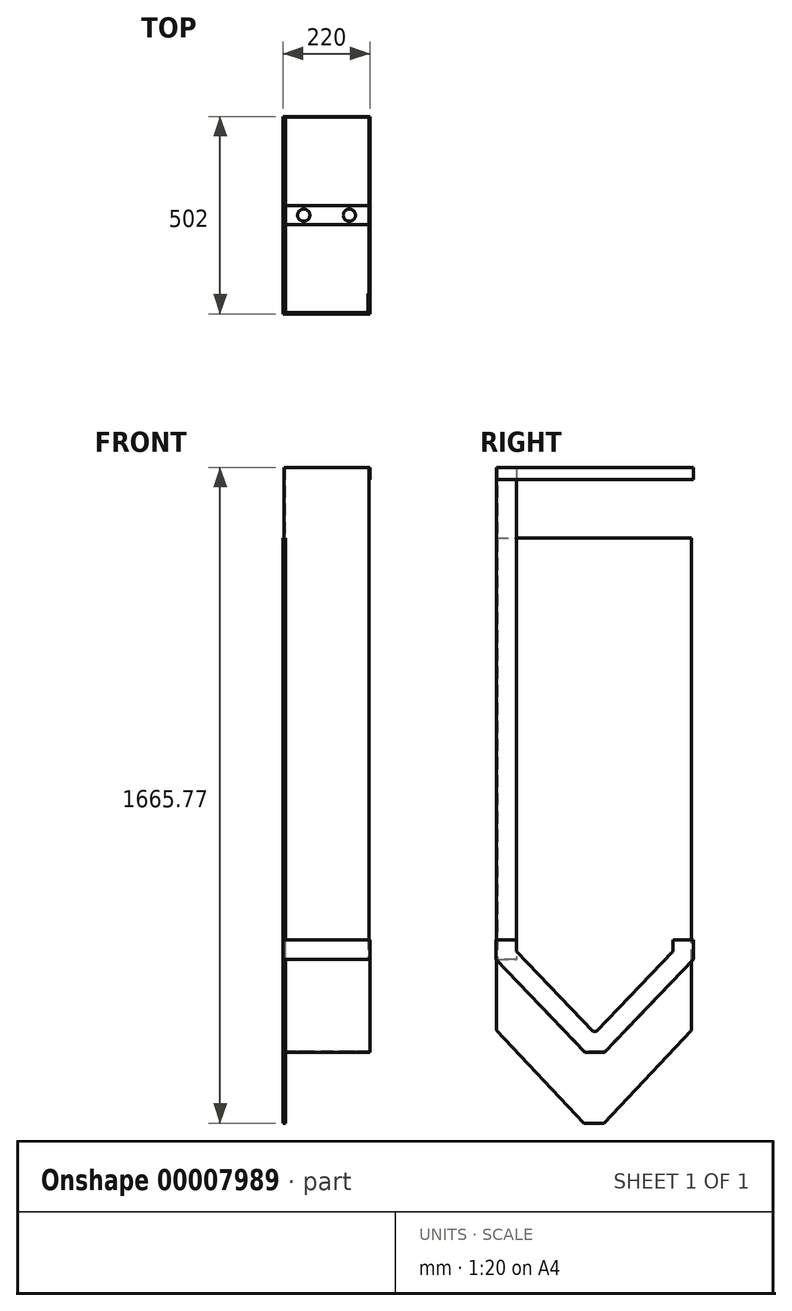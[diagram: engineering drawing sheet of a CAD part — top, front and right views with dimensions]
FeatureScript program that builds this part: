
annotation { "Feature Type Name" : "Feature", "Feature Type Description" : "" }
export const myFeature = defineFeature(function(context is Context, id is Id, definition is map)
    precondition{}
    {
        {
            var Q0;
            Q0=qCreatedBy(makeId("Right.planeOp"),FACE);
            var sketch = newSketch(context, id + "F0", { "sketchPlane" : qUnion([Q0])});
            skLineSegment(sketch, "E0", {"start": v(949.6, -192.94) * mm, "end": v(949.6, -142.94) * mm});
            skLineSegment(sketch, "E1", {"start": v(949.6, -192.94) * mm, "end": v(723.6, -428.58) * mm});
            skLineSegment(sketch, "E2", {"start": v(723.6, -428.58) * mm, "end": v(698.6, -428.58) * mm});
            skLineSegment(sketch, "E3", {"start": v(949.6, -142.94) * mm, "end": v(947.6, -142.94) * mm});
            skLineSegment(sketch, "E4", {"start": v(947.6, -142.94) * mm, "end": v(947.6, -192.13) * mm});
            skLineSegment(sketch, "E5", {"start": v(947.6, -192.13) * mm, "end": v(722.74, -426.58) * mm});
            skLineSegment(sketch, "E6", {"start": v(722.74, -426.58) * mm, "end": v(698.6, -426.58) * mm});
            skLineSegment(sketch, "E7", {"start": v(698.6, -426.58) * mm, "end": v(698.6, -390.33) * mm, "construction": true});
            skLineSegment(sketch, "E8", {"start": v(698.6, -426.58) * mm, "end": v(698.6, -449.98) * mm});
            skLineSegment(sketch, "E9.MirrorCS", {"start": v(673.6, -428.58) * mm, "end": v(698.6, -428.58) * mm});
            skLineSegment(sketch, "E10.MirrorCS", {"start": v(674.45, -426.58) * mm, "end": v(698.6, -426.58) * mm});
            skLineSegment(sketch, "E11.MirrorCS", {"start": v(449.6, -192.13) * mm, "end": v(674.45, -426.58) * mm});
            skLineSegment(sketch, "E12.MirrorCS", {"start": v(447.6, -192.94) * mm, "end": v(673.6, -428.58) * mm});
            skLineSegment(sketch, "E13.MirrorCS", {"start": v(449.6, -142.94) * mm, "end": v(449.6, -192.13) * mm});
            skLineSegment(sketch, "E14.MirrorCS", {"start": v(447.6, -192.94) * mm, "end": v(447.6, -142.94) * mm});
            skLineSegment(sketch, "E15.MirrorCS", {"start": v(447.6, -142.94) * mm, "end": v(449.6, -142.94) * mm});
            skSolve(sketch);
        }
        {
            var Q0;
            Q0=makeQuery(id+"F0.imprint","IMPRINT",FACE,{"disambiguationData":[TD([[makeQuery(id+"F0.imprint","IMPRINT",EDGE,{"derivedFrom":sQuery(id+"F0.wireOp",EDGE,"E0")}),1.0]])]});
            var Q1;
            {var subQ1=sQuery(id+"F0.wireOp",EDGE,"E9.MirrorCS");Q1=makeQuery(id+"F0.imprint","IMPRINT",FACE,{"disambiguationData":[TD([[makeQuery(id+"F0.imprint","IMPRINT",EDGE,{"derivedFrom":subQ1}),1.0]])]});}
            extrude(context, id + "F1", {"entities" : qUnion([Q0, Q1]), "depth" : 220 * mm});
        }
        {
            var Q0;
            Q0=qCreatedBy(makeId("Right.planeOp"),FACE);
            var sketch = newSketch(context, id + "F2", { "sketchPlane" : qUnion([Q0])});
            skLineSegment(sketch, "E16", {"start": v(947.6, -142.94) * mm, "end": v(897.6, -142.94) * mm});
            skLineSegment(sketch, "E17", {"start": v(898.91, -170.66) * mm, "end": v(702.8, -375.14) * mm});
            skLineSegment(sketch, "E18", {"start": v(698.6, -348.8) * mm, "end": v(698.6, -460.7) * mm, "construction": true});
            skLineSegment(sketch, "E19.MirrorCS", {"start": v(449.6, -142.94) * mm, "end": v(499.6, -142.94) * mm});
            skLineSegment(sketch, "E20.0", {"start": v(947.6, -192.13) * mm, "end": v(722.74, -426.58) * mm});
            skLineSegment(sketch, "E21.MirrorCS", {"start": v(449.6, -192.13) * mm, "end": v(674.45, -426.58) * mm});
            skLineSegment(sketch, "E22.MirrorCS", {"start": v(722.74, -426.58) * mm, "end": v(674.45, -426.58) * mm});
            skLineSegment(sketch, "E23", {"start": v(722.74, -426.58) * mm, "end": v(702.8, -375.14) * mm});
            skLineSegment(sketch, "E24", {"start": v(702.8, -375.14) * mm, "end": v(698.6, -375.14) * mm});
            skLineSegment(sketch, "E25.MirrorCS", {"start": v(694.4, -375.14) * mm, "end": v(698.6, -375.14) * mm});
            skLineSegment(sketch, "E26.MirrorCS", {"start": v(498.28, -170.66) * mm, "end": v(694.4, -375.14) * mm});
            skLineSegment(sketch, "E27", {"start": v(947.6, -192.13) * mm, "end": v(898.91, -170.66) * mm});
            skLineSegment(sketch, "E28.MirrorCS", {"start": v(674.45, -426.58) * mm, "end": v(694.4, -375.14) * mm});
            skLineSegment(sketch, "E29.MirrorCS", {"start": v(449.6, -192.13) * mm, "end": v(498.28, -170.66) * mm});
            skLineSegment(sketch, "E30", {"start": v(449.6, -142.94) * mm, "end": v(449.6, -192.13) * mm});
            skLineSegment(sketch, "E31.MirrorCS", {"start": v(947.6, -142.94) * mm, "end": v(947.6, -192.13) * mm});
            skLineSegment(sketch, "E32", {"start": v(897.6, -142.94) * mm, "end": v(897.6, -172.03) * mm});
            skLineSegment(sketch, "E33.MirrorCS", {"start": v(499.6, -142.94) * mm, "end": v(499.6, -172.03) * mm});
            skSolve(sketch);
        }
        {
            var Q0;
            Q0=makeQuery(id+"F2.imprint","IMPRINT",FACE,{"disambiguationData":[TD([[makeQuery(id+"F2.imprint","IMPRINT",EDGE,{"derivedFrom":sQuery(id+"F2.wireOp",EDGE,"E16")}),1.0]])]});
            var Q1;
            Q1=makeQuery(id+"F2.imprint","IMPRINT",FACE,{"disambiguationData":[TD([[makeQuery(id+"F2.imprint","IMPRINT",EDGE,{"derivedFrom":sQuery(id+"F2.wireOp",EDGE,"E17")}),1.0]])]});
            var Q2;
            Q2=makeQuery(id+"F2.imprint","IMPRINT",FACE,{"disambiguationData":[TD([[makeQuery(id+"F2.imprint","IMPRINT",EDGE,{"derivedFrom":sQuery(id+"F2.wireOp",EDGE,"E19.MirrorCS")}),-1.0]])]});
            var Q3;
            Q3=makeQuery(id+"F2.imprint","IMPRINT",FACE,{"disambiguationData":[TD([[makeQuery(id+"F2.imprint","IMPRINT",EDGE,{"derivedFrom":sQuery(id+"F2.wireOp",EDGE,"E21.MirrorCS")}),1.0]])]});
            var Q4;
            Q4=makeQuery(id+"F2.imprint","IMPRINT",FACE,{"disambiguationData":[TD([[makeQuery(id+"F2.imprint","IMPRINT",EDGE,{"derivedFrom":sQuery(id+"F2.wireOp",EDGE,"331c9890-ce68-4b07-ae29-14cf17e063d5")}),1.0]])]});
            var Q5;
            Q5=makeQuery(id+"F2.imprint","IMPRINT",FACE,{"disambiguationData":[TD([[makeQuery(id+"F2.imprint","IMPRINT",EDGE,{"derivedFrom":sQuery(id+"F2.wireOp",EDGE,"E22.MirrorCS")}),-1.0]])]});
            extrude(context, id + "F3", {"entities" : qUnion([Q0, Q1, Q2, Q3, Q4, Q5]), "depth" : 2 * mm});
        }
        {
            var Q0;
            Q0=makeQuery(id+"F3.opExtrude","SWEPT_BODY",BODY,{"disambiguationData":[OSD([sQuery(id+"F2.wireOp",EDGE,"E16"),sQuery(id+"F2.wireOp",EDGE,"91f219d3-7e8a-4c19-a2bf-eaeb5ddfdd50"),sQuery(id+"F2.wireOp",EDGE,"E17"),sQuery(id+"F2.wireOp",EDGE,"f22f1ab5-6c7a-48bc-a4eb-af161df78c79"),sQuery(id+"F2.wireOp",EDGE,"e779fc2c-cb4b-4187-b623-f86fede4607c0.MirrorCS"),sQuery(id+"F2.wireOp",EDGE,"E19.MirrorCS"),sQuery(id+"F2.wireOp",EDGE,"f3476c4e-f956-4570-b143-a2dea3c2c5ab0.MirrorCS"),sQuery(id+"F2.wireOp",EDGE,"1e2c1291-7e1b-4bd3-b756-017ac6b8f697"),sQuery(id+"F2.wireOp",EDGE,"544c7c23-52e5-48f1-b12a-f50e7f1eaf0e"),sQuery(id+"F2.wireOp",EDGE,"331c9890-ce68-4b07-ae29-14cf17e063d5"),sQuery(id+"F2.wireOp",EDGE,"E21.MirrorCS"),sQuery(id+"F2.wireOp",EDGE,"E22.MirrorCS"),sQuery(id+"F2.wireOp",EDGE,"362d2f28-4ba6-4a2b-b450-6a094d1aa8730.MirrorCS")])]});
            transform(context, id + "F4", {"entities" : qUnion([Q0]), "transformType" : TransformType.TRANSLATION_3D, "dx" : 218 * mm, "dy" : 0 * mm, "dz" : 0 * mm, "makeCopy" : true});
        }
        {
            var Q0;
            Q0=makeQuery(id+"F1.opExtrude","SWEPT_BODY",BODY,{"disambiguationData":[OSD([sQuery(id+"F0.wireOp",EDGE,"E0"),sQuery(id+"F0.wireOp",EDGE,"E1"),sQuery(id+"F0.wireOp",EDGE,"E2"),sQuery(id+"F0.wireOp",EDGE,"E3"),sQuery(id+"F0.wireOp",EDGE,"E4"),sQuery(id+"F0.wireOp",EDGE,"E5"),sQuery(id+"F0.wireOp",EDGE,"E6"),sQuery(id+"F0.wireOp",EDGE,"E9.MirrorCS"),sQuery(id+"F0.wireOp",EDGE,"E10.MirrorCS"),sQuery(id+"F0.wireOp",EDGE,"E11.MirrorCS"),sQuery(id+"F0.wireOp",EDGE,"E12.MirrorCS"),sQuery(id+"F0.wireOp",EDGE,"E13.MirrorCS"),sQuery(id+"F0.wireOp",EDGE,"E14.MirrorCS"),sQuery(id+"F0.wireOp",EDGE,"E15.MirrorCS")])]});
            var Q1;
            Q1=makeQuery(id+"F3.opExtrude","SWEPT_BODY",BODY,{"disambiguationData":[OSD([sQuery(id+"F2.wireOp",EDGE,"E16"),sQuery(id+"F2.wireOp",EDGE,"91f219d3-7e8a-4c19-a2bf-eaeb5ddfdd50"),sQuery(id+"F2.wireOp",EDGE,"E17"),sQuery(id+"F2.wireOp",EDGE,"f22f1ab5-6c7a-48bc-a4eb-af161df78c79"),sQuery(id+"F2.wireOp",EDGE,"e779fc2c-cb4b-4187-b623-f86fede4607c0.MirrorCS"),sQuery(id+"F2.wireOp",EDGE,"E19.MirrorCS"),sQuery(id+"F2.wireOp",EDGE,"f3476c4e-f956-4570-b143-a2dea3c2c5ab0.MirrorCS"),sQuery(id+"F2.wireOp",EDGE,"1e2c1291-7e1b-4bd3-b756-017ac6b8f697"),sQuery(id+"F2.wireOp",EDGE,"544c7c23-52e5-48f1-b12a-f50e7f1eaf0e"),sQuery(id+"F2.wireOp",EDGE,"331c9890-ce68-4b07-ae29-14cf17e063d5"),sQuery(id+"F2.wireOp",EDGE,"E21.MirrorCS"),sQuery(id+"F2.wireOp",EDGE,"E22.MirrorCS"),sQuery(id+"F2.wireOp",EDGE,"362d2f28-4ba6-4a2b-b450-6a094d1aa8730.MirrorCS")])]});
            var Q2;
            Q2=makeQuery(id+"F4.opPattern","COPY",BODY,{"derivedFrom":makeQuery(id+"F3.opExtrude","SWEPT_BODY",BODY,{"disambiguationData":[OSD([sQuery(id+"F2.wireOp",EDGE,"E16"),sQuery(id+"F2.wireOp",EDGE,"91f219d3-7e8a-4c19-a2bf-eaeb5ddfdd50"),sQuery(id+"F2.wireOp",EDGE,"E17"),sQuery(id+"F2.wireOp",EDGE,"f22f1ab5-6c7a-48bc-a4eb-af161df78c79"),sQuery(id+"F2.wireOp",EDGE,"e779fc2c-cb4b-4187-b623-f86fede4607c0.MirrorCS"),sQuery(id+"F2.wireOp",EDGE,"E19.MirrorCS"),sQuery(id+"F2.wireOp",EDGE,"f3476c4e-f956-4570-b143-a2dea3c2c5ab0.MirrorCS"),sQuery(id+"F2.wireOp",EDGE,"1e2c1291-7e1b-4bd3-b756-017ac6b8f697"),sQuery(id+"F2.wireOp",EDGE,"544c7c23-52e5-48f1-b12a-f50e7f1eaf0e"),sQuery(id+"F2.wireOp",EDGE,"331c9890-ce68-4b07-ae29-14cf17e063d5"),sQuery(id+"F2.wireOp",EDGE,"E21.MirrorCS"),sQuery(id+"F2.wireOp",EDGE,"E22.MirrorCS"),sQuery(id+"F2.wireOp",EDGE,"362d2f28-4ba6-4a2b-b450-6a094d1aa8730.MirrorCS")])]}),"instanceName":"1"});
            booleanBodies(context, id + "F5", {"operationType" : BooleanOperationType.UNION, "tools" : qUnion([Q0, Q1, Q2])});
        }
        {
            var Q0;
            Q0=makeQuery(id+"F1.opExtrude","SWEPT_FACE",FACE,{"disambiguationData":[OSD([sQuery(id+"F0.wireOp",EDGE,"E6"),sQuery(id+"F0.wireOp",EDGE,"E10.MirrorCS")])]});
            var sketch = newSketch(context, id + "F6", { "sketchPlane" : qUnion([Q0])});
            skCircle(sketch, "E34", {"center": v(52, 698.6) * mm, "radius": 15.5 * mm});
            skCircle(sketch, "E35", {"center": v(168, 698.6) * mm, "radius": 15.5 * mm});
            skLineSegment(sketch, "E36", {"start": v(2, 698.6) * mm, "end": v(218, 698.6) * mm, "construction": true});
            skLineSegment(sketch, "E37.top", {"start": v(3, 897.6) * mm, "end": v(2, 897.6) * mm});
            skSolve(sketch);
        }
        {
            var Q0;
            Q0=makeQuery(id+"F6.imprint","IMPRINT",FACE,{"disambiguationData":[TD([[makeQuery(id+"F6.imprint","IMPRINT",EDGE,{"derivedFrom":sQuery(id+"F6.wireOp",EDGE,"E34")}),1.0]])]});
            var Q1;
            Q1=makeQuery(id+"F6.imprint","IMPRINT",FACE,{"disambiguationData":[TD([[makeQuery(id+"F6.imprint","IMPRINT",EDGE,{"derivedFrom":sQuery(id+"F6.wireOp",EDGE,"E35")}),1.0]])]});
            extrude(context, id + "F7", {"entities" : qUnion([Q0, Q1]), "operationType" : NewBodyOperationType.REMOVE, "endBound" : BoundingType.THROUGH_ALL, "oppositeDirection" : true, "depth" : 25 * mm});
        }
        {
            var Q0;
            Q0=qCreatedBy(makeId("Right.planeOp"),FACE);
            var sketch = newSketch(context, id + "F8", { "sketchPlane" : qUnion([Q0])});
            skLineSegment(sketch, "E38.top", {"start": v(448.98, 877.24) * mm, "end": v(944.98, 877.24) * mm});
            skLineSegment(sketch, "E38.left", {"start": v(448.98, -372.76) * mm, "end": v(448.98, 877.24) * mm});
            skLineSegment(sketch, "E38.right", {"start": v(944.98, -372.76) * mm, "end": v(944.98, 877.24) * mm});
            skLineSegment(sketch, "E39", {"start": v(696.98, -181.11) * mm, "end": v(696.98, -469.75) * mm, "construction": true});
            skLineSegment(sketch, "E40", {"start": v(671.98, -608.71) * mm, "end": v(448.98, -372.76) * mm});
            skLineSegment(sketch, "E41", {"start": v(696.98, 877.24) * mm, "end": v(696.98, -181.11) * mm, "construction": true});
            skLineSegment(sketch, "E42", {"start": v(179.2, -372.76) * mm, "end": v(1345.43, -372.76) * mm, "construction": true});
            skLineSegment(sketch, "E43", {"start": v(671.98, -608.71) * mm, "end": v(721.98, -608.71) * mm});
            skLineSegment(sketch, "E44.bottom", {"start": v(2145.92, 823.15) * mm, "end": v(2894.1, 823.15) * mm});
            skLineSegment(sketch, "E44.top", {"start": v(2145.92, 0) * mm, "end": v(2894.1, 0) * mm});
            skLineSegment(sketch, "E44.left", {"start": v(2145.92, 823.15) * mm, "end": v(2145.92, 0) * mm});
            skLineSegment(sketch, "E44.right", {"start": v(2894.1, 823.15) * mm, "end": v(2894.1, 0) * mm});
            skPoint(sketch, "E45", {"position": v(696.98, -608.71) * mm});
            skLineSegment(sketch, "E46", {"start": v(721.98, -608.71) * mm, "end": v(944.98, -372.76) * mm});
            skSolve(sketch);
        }
        {
            var Q0;
            {var subQ11=sQuery(id+"F8.wireOp",EDGE,"E38.top");Q0=makeQuery(id+"F8.imprint","IMPRINT",FACE,{"disambiguationData":[TD([[makeQuery(id+"F8.imprint","IMPRINT",EDGE,{"derivedFrom":subQ11}),-1.0]])]});}
            var Q1;
            {var subQ3=makeQuery(id+"F4.opPattern","COPY",EDGE,{"derivedFrom":makeQuery(id+"F3.opExtrude","CAP_EDGE",EDGE,{"disambiguationData":[OSD([sQuery(id+"F2.wireOp",EDGE,"ecf41299-9a6b-420b-9139-a0777f581a70")])],"isStart":true}),"instanceName":"1"});Q1=makeQuery(id+"F8.imprint","IMPRINT",FACE,{"disambiguationData":[TD([[makeQuery(id+"F8.imprint","IMPRINT",EDGE,{"derivedFrom":subQ3}),-1.0]])]});}
            var Q2;
            Q2=makeQuery(id+"F8.imprint","IMPRINT",FACE,{"disambiguationData":[TD([[makeQuery(id+"F8.imprint","IMPRINT",EDGE,{"derivedFrom":sQuery(id+"F8.wireOp",EDGE,"1a1e0056-a2cf-43d9-bfc2-85c644d87007")}),1.0]])]});
            var Q3;
            {var subQ3=makeQuery(id+"F4.opPattern","COPY",EDGE,{"derivedFrom":makeQuery(id+"F3.opExtrude","CAP_EDGE",EDGE,{"disambiguationData":[OSD([sQuery(id+"F2.wireOp",EDGE,"E24"),sQuery(id+"F2.wireOp",EDGE,"E25.MirrorCS")])],"isStart":true}),"instanceName":"1"});Q3=makeQuery(id+"F8.imprint","IMPRINT",FACE,{"disambiguationData":[TD([[makeQuery(id+"F8.imprint","IMPRINT",EDGE,{"derivedFrom":subQ3}),1.0]])]});}
            var Q4;
            {var subQ3=makeQuery(id+"F4.opPattern","COPY",EDGE,{"derivedFrom":makeQuery(id+"F3.opExtrude","CAP_EDGE",EDGE,{"disambiguationData":[OSD([sQuery(id+"F2.wireOp",EDGE,"970c18d3-8c09-4add-8954-55657481e7b40.MirrorCS")])],"isStart":true}),"instanceName":"1"});Q4=makeQuery(id+"F8.imprint","IMPRINT",FACE,{"disambiguationData":[TD([[makeQuery(id+"F8.imprint","IMPRINT",EDGE,{"derivedFrom":subQ3}),1.0]])]});}
            extrude(context, id + "F9", {"entities" : qUnion([Q0, Q1, Q2, Q3, Q4]), "depth" : 6 * mm});
        }
        {
            var Q0;
            {var subQ0=makeQuery(id+"F3.opExtrude","SWEPT_FACE",FACE,{"disambiguationData":[OSD([sQuery(id+"F2.wireOp",EDGE,"E19.MirrorCS")])]});Q0=makeQuery(id+"F5.opBoolean","MERGE",FACE,{"derivedFrom":[makeQuery(id+"F1.opExtrude","SWEPT_FACE",FACE,{"disambiguationData":[OSD([sQuery(id+"F0.wireOp",EDGE,"E15.MirrorCS")])]}),subQ0,makeQuery(id+"F4.opPattern","COPY",FACE,{"derivedFrom":subQ0,"instanceName":"1"})]});}
            cPlane(context, id + "F10", {"entities" : qUnion([Q0]), "cplaneType" : CPlaneType.OFFSET, "offset" : 50 * mm, "oppositeDirection" : true, "width" : 150 * mm, "height" : 150 * mm});
        }
        {
            var Q0;
            Q0=qCreatedBy(id+"F10.planeOp",FACE);
            var sketch = newSketch(context, id + "F11", { "sketchPlane" : qUnion([Q0])});
            skLineSegment(sketch, "E47", {"start": v(218, 499.6) * mm, "end": v(216, 499.6) * mm});
            skLineSegment(sketch, "E48", {"start": v(216, 499.6) * mm, "end": v(216, 451.6) * mm});
            skLineSegment(sketch, "E49", {"start": v(216, 451.6) * mm, "end": v(4, 451.6) * mm});
            skLineSegment(sketch, "E50", {"start": v(4, 451.6) * mm, "end": v(4, 499.6) * mm});
            skLineSegment(sketch, "E51", {"start": v(4, 499.6) * mm, "end": v(2, 499.6) * mm});
            skLineSegment(sketch, "E52", {"start": v(2, 499.6) * mm, "end": v(2, 449.6) * mm});
            skLineSegment(sketch, "E53", {"start": v(2, 449.6) * mm, "end": v(218, 449.6) * mm});
            skLineSegment(sketch, "E54", {"start": v(218, 449.6) * mm, "end": v(218, 499.6) * mm});
            skLineSegment(sketch, "E55.bottom", {"start": v(220, 447.6) * mm, "end": v(218, 447.6) * mm});
            skLineSegment(sketch, "E55.top", {"start": v(220, 449.6) * mm, "end": v(218, 449.6) * mm});
            skLineSegment(sketch, "E55.left", {"start": v(220, 447.6) * mm, "end": v(220, 449.6) * mm});
            skLineSegment(sketch, "E55.right", {"start": v(218, 447.6) * mm, "end": v(218, 449.6) * mm});
            skSolve(sketch);
        }
        {
            var Q0;
            Q0=makeQuery(id+"F11.imprint","IMPRINT",FACE,{"disambiguationData":[TD([[makeQuery(id+"F11.imprint","IMPRINT",EDGE,{"derivedFrom":sQuery(id+"F11.wireOp",EDGE,"E47")}),1.0]])]});
            extrude(context, id + "F12", {"entities" : qUnion([Q0]), "depth" : 1250 * mm});
        }
        {
            var Q0;
            Q0=makeQuery(id+"F12.opExtrude","SWEPT_FACE",FACE,{"disambiguationData":[OSD([sQuery(id+"F11.wireOp",EDGE,"E54")])]});
            var sketch = newSketch(context, id + "F13", { "sketchPlane" : qUnion([Q0])});
            skLineSegment(sketch, "E56.bottom", {"start": v(449.6, 1057.06) * mm, "end": v(949.6, 1057.06) * mm});
            skLineSegment(sketch, "E56.top", {"start": v(449.6, 1027.06) * mm, "end": v(949.6, 1027.06) * mm});
            skLineSegment(sketch, "E56.left", {"start": v(449.6, 1057.06) * mm, "end": v(449.6, 1027.06) * mm});
            skLineSegment(sketch, "E56.right", {"start": v(949.6, 1057.06) * mm, "end": v(949.6, 1027.06) * mm});
            skSolve(sketch);
        }
        {
            var Q0;
            Q0 = qSketchRegion(id + "F13", true);
            extrude(context, id + "F14", {"entities" : qUnion([Q0]), "depth" : 2 * mm});
        }
    });
